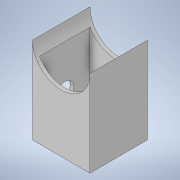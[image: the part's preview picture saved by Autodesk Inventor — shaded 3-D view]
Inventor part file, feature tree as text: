
AUTODESK INVENTOR PART (.ipt)
format: ipt  version: 2021 (Build 250183000, 183)  size: 119,296 bytes
history: native  units: in
note: dims shown in document units (in); Inventor stores cm internally (conversion verified against a paired STEP export)
features: extrude x3, sketch x3
ambient origin geometry x8: Origin, YZ Plane, XZ Plane, XY Plane, X Axis, Y Axis, Z Axis, Center Point
bodies: Body1 (feature_tree)
feature tree (6):
  extrude  "Extrusion2"  Depth=1.0in
  extrude  "Extrusion4"  Depth=0.9375in
  extrude  "Extrusion6"  Depth=0.875in
  sketch  "Sketch3"  dims[d4=1.0in d5=1.0in]
  sketch  "Sketch5"  dims[d6=0.0625in d7=0.9375in]
  sketch  "Sketch8"  dims[d8=0.875in d9=0.875in d10=1.5in d11=0.0in d16=1.0in d17=0.0in d22=0.313in d23=0.5in d24=0.0in]
